FCSTD DOCUMENT  (FreeCAD 0.17R11223 (Git))
Label: Crystal_SMD_TXC_8045-2Pin_8.0x4.5mm_01
License: All rights reserved
LicenseURL: http://en.wikipedia.org/wiki/All_rights_reserved
objects: Sketcher::SketchObject×1
note: 1 computed .brp shape members not serialized (recipe doc carries the construction recipe); baked Part::Feature solids carry a one-line shape summary decoded from their .brp

FEATURE [Sketcher::SketchObject] Sketch
  sketch-geometry (16):
    g0: ArcOfCircle CenterX=-4 CenterY=-2.25 CenterZ=0 NormalX=0 NormalY=0 NormalZ=1 Radius=0.5 StartAngle=0 EndAngle=1.5708
    g1: ArcOfCircle CenterX=4 CenterY=2.25 CenterZ=0 NormalX=0 NormalY=0 NormalZ=1 Radius=0.5 StartAngle=3.14159 EndAngle=4.71239
    g2: ArcOfCircle CenterX=4 CenterY=-2.25 CenterZ=0 NormalX=0 NormalY=0 NormalZ=1 Radius=0.5 StartAngle=1.5708 EndAngle=3.14159
    g3: LineSegment StartX=-3.5 StartY=2.25 StartZ=0 EndX=3.5 EndY=2.25 EndZ=0
    g4: ArcOfCircle CenterX=4 CenterY=0.6 CenterZ=0 NormalX=0 NormalY=0 NormalZ=1 Radius=0.25 StartAngle=1.5708 EndAngle=3.14159
    g5: ArcOfCircle CenterX=4 CenterY=-0.6 CenterZ=0 NormalX=0 NormalY=0 NormalZ=1 Radius=0.25 StartAngle=3.14159 EndAngle=4.71239
    g6: ArcOfCircle CenterX=-4 CenterY=0.6 CenterZ=0 NormalX=0 NormalY=0 NormalZ=1 Radius=0.25 StartAngle=0 EndAngle=1.5708
    g7: ArcOfCircle CenterX=-4 CenterY=-0.6 CenterZ=0 NormalX=0 NormalY=0 NormalZ=1 Radius=0.25 StartAngle=4.71239 EndAngle=6.28319
    g8: LineSegment StartX=-3.5 StartY=-2.25 StartZ=0 EndX=3.5 EndY=-2.25 EndZ=0
    g9: LineSegment StartX=4 StartY=-1.75 StartZ=0 EndX=4 EndY=-0.85 EndZ=0
    g10: LineSegment StartX=3.75 StartY=-0.6 StartZ=0 EndX=3.75 EndY=0.6 EndZ=0
    g11: LineSegment StartX=4 StartY=1.75 StartZ=0 EndX=4 EndY=0.85 EndZ=0
    g12: LineSegment StartX=-4 StartY=-1.75 StartZ=0 EndX=-4 EndY=-0.85 EndZ=0
    g13: LineSegment StartX=-3.75 StartY=0.6 StartZ=0 EndX=-3.75 EndY=-0.6 EndZ=0
    g14: ArcOfCircle CenterX=-4 CenterY=2.25 CenterZ=0 NormalX=0 NormalY=0 NormalZ=1 Radius=0.5 StartAngle=4.71239 EndAngle=6.28319
    g15: LineSegment StartX=-4 StartY=1.75 StartZ=0 EndX=-4 EndY=0.85 EndZ=0
  constraints (56):
    c: Coincident(g3,g1)
    c: Horizontal(g3)
    c: DistanceY(g0,g0) = 0
    c: DistanceX(g0,g0) = 0
    c: DistanceY(g1,g1) = 0
    c: DistanceX(g1,g1) = 0
    c: DistanceX(g2,g2) = 0
    c: DistanceY(g2,g2) = 0
    c: DistanceY(g7,g7) = 0
    c: DistanceX(g7,g7) = 0
    c: DistanceX(g6,g6) = 0
    c: DistanceY(g6,g6) = 0
    c: DistanceY(g4,g4) = 0
    c: DistanceX(g4,g4) = 0
    c: DistanceX(g5,g5) = 0
    c: Coincident(g8,g0)
    c: Coincident(g8,g2)
    c: Coincident(g9,g2)
    c: Coincident(g9,g5)
    c: Coincident(g10,g5)
    c: Coincident(g10,g4)
    c: Coincident(g11,g1)
    c: Coincident(g11,g4)
    c: Vertical(g11)
    c: Coincident(g12,g0)
    c: Coincident(g12,g7)
    c: Coincident(g13,g6)
    c: Coincident(g13,g7)
    c: DistanceX(g6,g7) = 0
    c: DistanceX(g0,g7) = 0
    c: DistanceY(g2,g0) = 0
    c: DistanceX(g2,g5) = 0
    c: DistanceX(g5,g4) = 0
    c: Radius(g6) = 0.25
    c: Equal(g6,g7)
    c: Equal(g6,g4)
    c: Equal(g6,g5)
    c: DistanceY(g5,g5) = 0
    c: DistanceY(g2,g1) = 4.5
    c: DistanceY(g5,g4) = 1.7
    c: DistanceY(g7,g6) = 1.7
    c: Coincident(g14,g3)
    c: Coincident(g15,g14)
    c: Coincident(g15,g6)
    c: DistanceX(g6,g14) = 0
    c: Radius(g14) = 0.5
    c: DistanceX(g14,g3) = 0.5
    c: DistanceY(g14,g3) = 0.5
    c: DistanceX(g1,g1) = 0.5
    c: DistanceX(g2,g2) = 0.5
    c: DistanceX(g0,g0) = 0.5
    c: DistanceY(g4,g1) = 1.4
    c: DistanceY(g6,g3) = 1.4
    c: DistanceX(g14,g1) = 8
    c: DistanceX(g6,g-1) = 4
    c: DistanceY(g-1,g3) = 2.25
